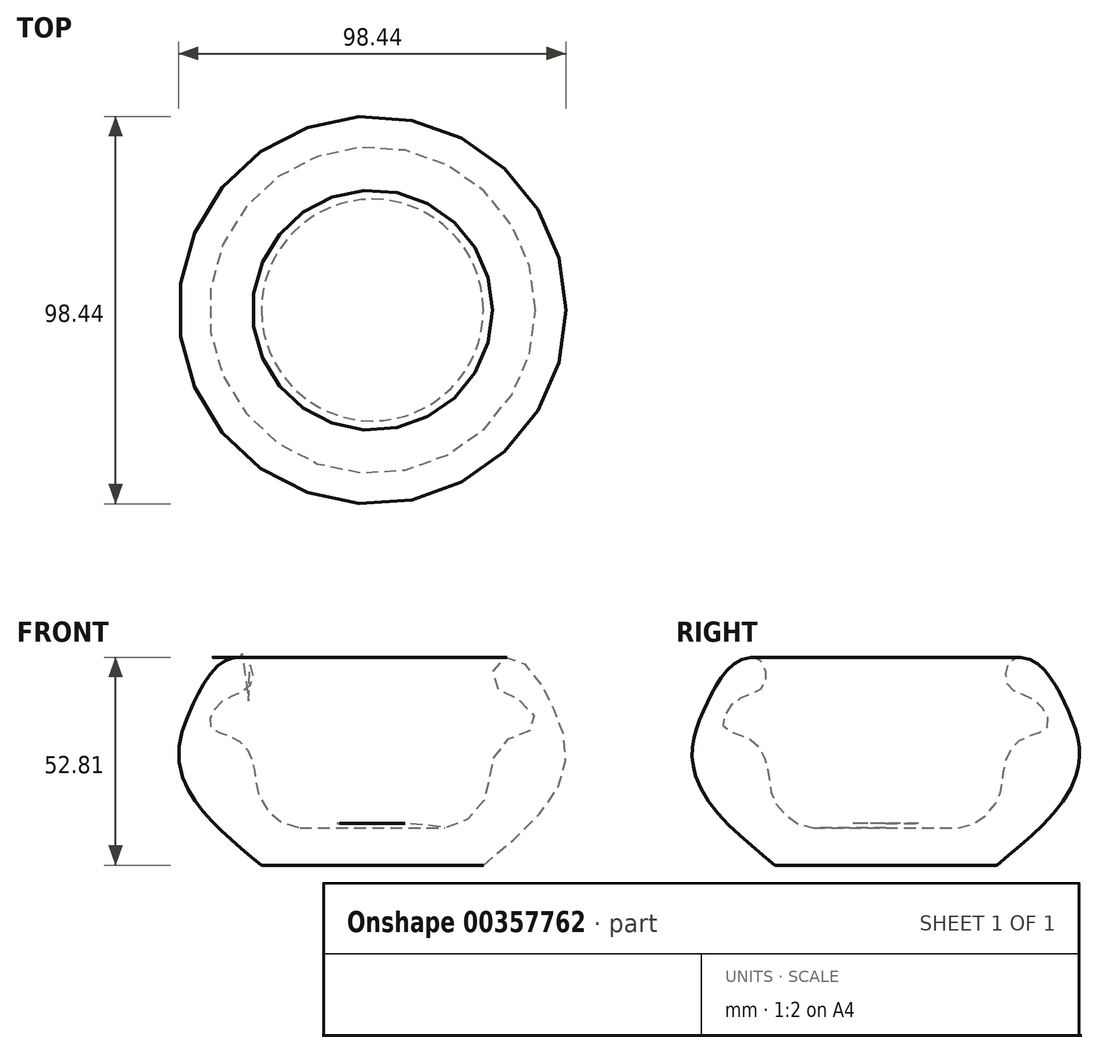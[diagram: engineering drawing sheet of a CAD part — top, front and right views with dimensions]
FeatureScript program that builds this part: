
annotation { "Feature Type Name" : "Feature", "Feature Type Description" : "" }
export const myFeature = defineFeature(function(context is Context, id is Id, definition is map)
    precondition{}
    {
        {
            var Q0;
            Q0=qCreatedBy(makeId("Front.planeOp"),FACE);
            var sketch = newSketch(context, id + "F0", { "sketchPlane" : qUnion([Q0])});
            skLineSegment(sketch, "E0", {"start": v(0, 0) * mm, "end": v(0, 10.16) * mm});
            skLineSegment(sketch, "E1", {"start": v(0, 0) * mm, "end": v(28.17, 0) * mm});
            skFitSpline(sketch, "E2", {"points": [v(28.17, 0) * mm, v(45.23, 16.5) * mm, v(49.2, 29.2) * mm, v(45.63, 40.7) * mm, v(38.49, 51.22) * mm, v(31.94, 52.02) * mm, v(31.15, 45.47) * mm, v(37.7, 41.9) * mm, v(41.26, 35.35) * mm, v(34.12, 31.78) * mm, v(29.96, 24.04) * mm, v(28.17, 16.1) * mm, v(20.43, 9.76) * mm, v(12.5, 10.36) * mm, v(0, 10.16) * mm], "startDerivative": vector(180.54, 148.08) * mm, "endDerivative": vector(-166.62, -12.7) * mm});
            skSolve(sketch);
        }
        {
            var Q0;
            Q0=makeQuery(id+"F0.imprint","IMPRINT",FACE,{"disambiguationData":[TD([[makeQuery(id+"F0.imprint","IMPRINT",EDGE,{"derivedFrom":sQuery(id+"F0.wireOp",EDGE,"E0")}),-1.0]])]});
            var Q1;
            Q1=sQuery(id+"F0.wireOp",EDGE,"E0");
            revolve(context, id + "F1", {"entities" : qUnion([Q0]), "axis" : qUnion([Q1]), "revolveType" : RevolveType.FULL});
        }
    });
